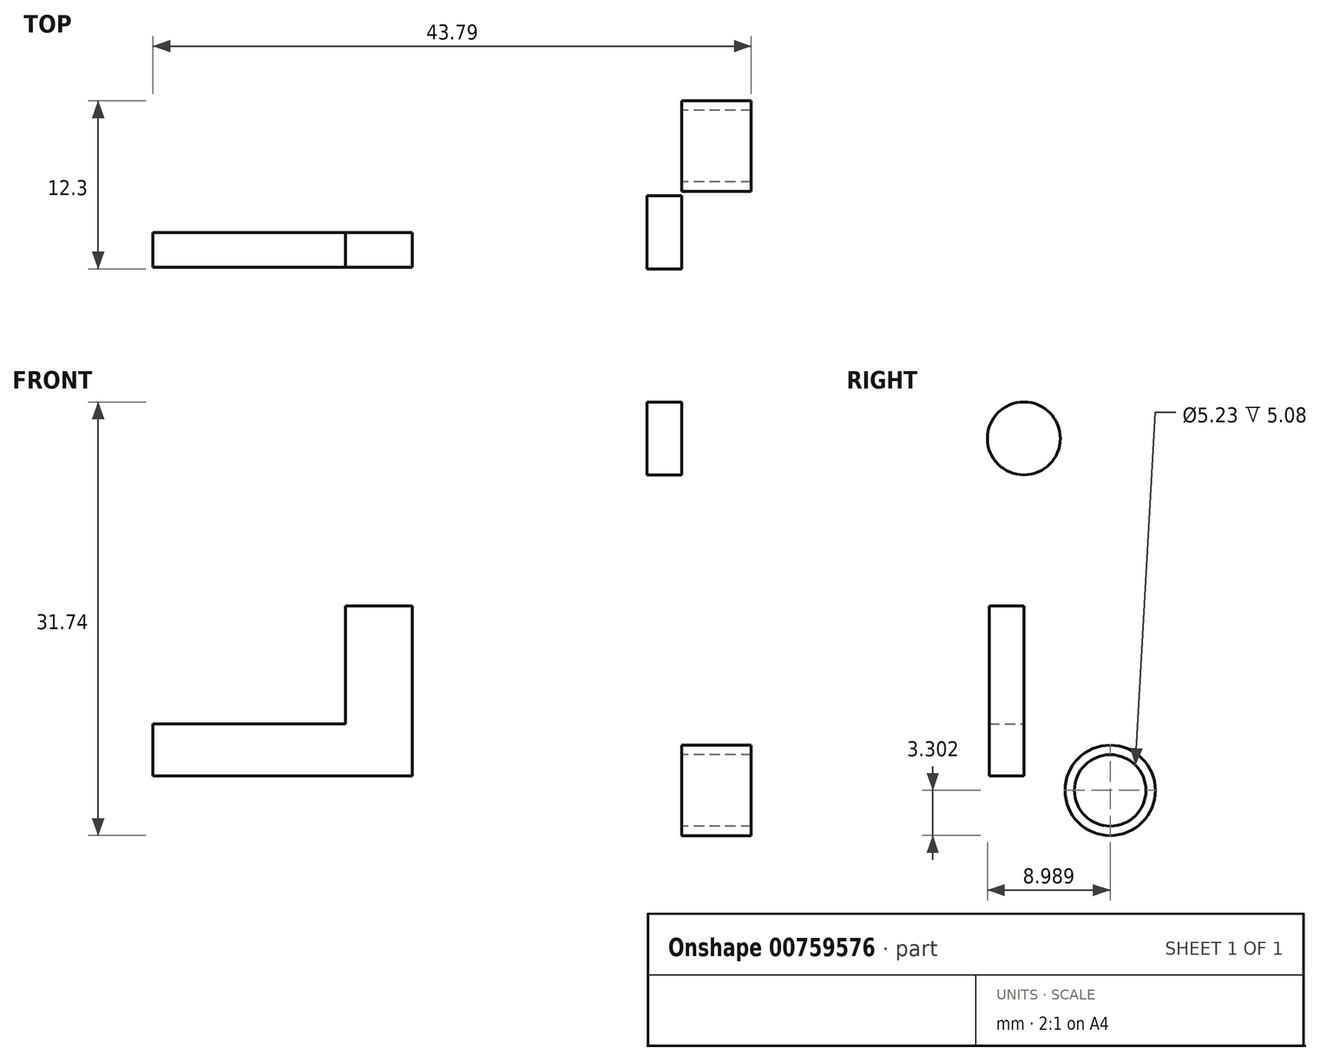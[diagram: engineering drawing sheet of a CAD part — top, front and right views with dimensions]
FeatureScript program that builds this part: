
annotation { "Feature Type Name" : "Feature", "Feature Type Description" : "" }
export const myFeature = defineFeature(function(context is Context, id is Id, definition is map)
    precondition{}
    {
        {
            var Q0;
            Q0=qCreatedBy(makeId("Front.planeOp"),FACE);
            var sketch = newSketch(context, id + "F0", { "sketchPlane" : qUnion([Q0])});
            skLineSegment(sketch, "E0", {"start": v(-38.7, 23.43) * mm, "end": v(-19.71, 23.43) * mm});
            skLineSegment(sketch, "E1", {"start": v(-19.71, 35.85) * mm, "end": v(-19.71, 23.43) * mm});
            skLineSegment(sketch, "E2", {"start": v(-19.71, 35.85) * mm, "end": v(-24.6, 35.85) * mm});
            skLineSegment(sketch, "E3", {"start": v(-24.6, 35.85) * mm, "end": v(-24.6, 31.25) * mm});
            skLineSegment(sketch, "E4", {"start": v(-24.6, 31.25) * mm, "end": v(-24.6, 27.22) * mm});
            skLineSegment(sketch, "E5", {"start": v(-38.7, 27.22) * mm, "end": v(-24.6, 27.22) * mm});
            skLineSegment(sketch, "E6", {"start": v(-38.7, 23.43) * mm, "end": v(-38.7, 27.22) * mm});
            skSolve(sketch);
        }
        {
            var Q0;
            Q0=qSketchRegion(id+"F0",true);
            extrude(context, id + "F1", {"entities" : qUnion([Q0]), "depth" : 2.54 * mm, "offsetDistance" : 25.4 * mm});
        }
        {
            var Q0;
            Q0=qCreatedBy(makeId("Right.planeOp"),FACE);
            var sketch = newSketch(context, id + "F2", { "sketchPlane" : qUnion([Q0])});
            skCircle(sketch, "E7", {"center": v(0, 48.13) * mm, "radius": 2.67 * mm});
            skSolve(sketch);
        }
        {
            var Q0;
            Q0=qSketchRegion(id+"F2",true);
            extrude(context, id + "F3", {"entities" : qUnion([Q0]), "oppositeDirection" : true, "depth" : 2.54 * mm, "offsetDistance" : 25.4 * mm});
        }
        {
            var Q0;
            Q0=qCreatedBy(makeId("Right.planeOp"),FACE);
            var sketch = newSketch(context, id + "F4", { "sketchPlane" : qUnion([Q0])});
            skCircle(sketch, "E8", {"center": v(6.32, 22.36) * mm, "radius": 2.61 * mm});
            skCircle(sketch, "E9", {"center": v(6.32, 22.36) * mm, "radius": 3.3 * mm});
            skSolve(sketch);
        }
        {
            var Q0;
            Q0=makeQuery(id+"F4.imprint","IMPRINT",FACE,{"disambiguationData":[TD([[makeQuery(id+"F4.imprint","IMPRINT",EDGE,{"derivedFrom":sQuery(id+"F4.wireOp",EDGE,"E8")}),-1.0]])]});
            var Q1;
            Q1=sQuery(id+"F4.wireOp",EDGE,"E9");
            extrude(context, id + "F5", {"entities" : qUnion([Q0]), "surfaceEntities" : qUnion([Q1]), "depth" : 5.08 * mm, "offsetDistance" : 25.4 * mm});
        }
    });
